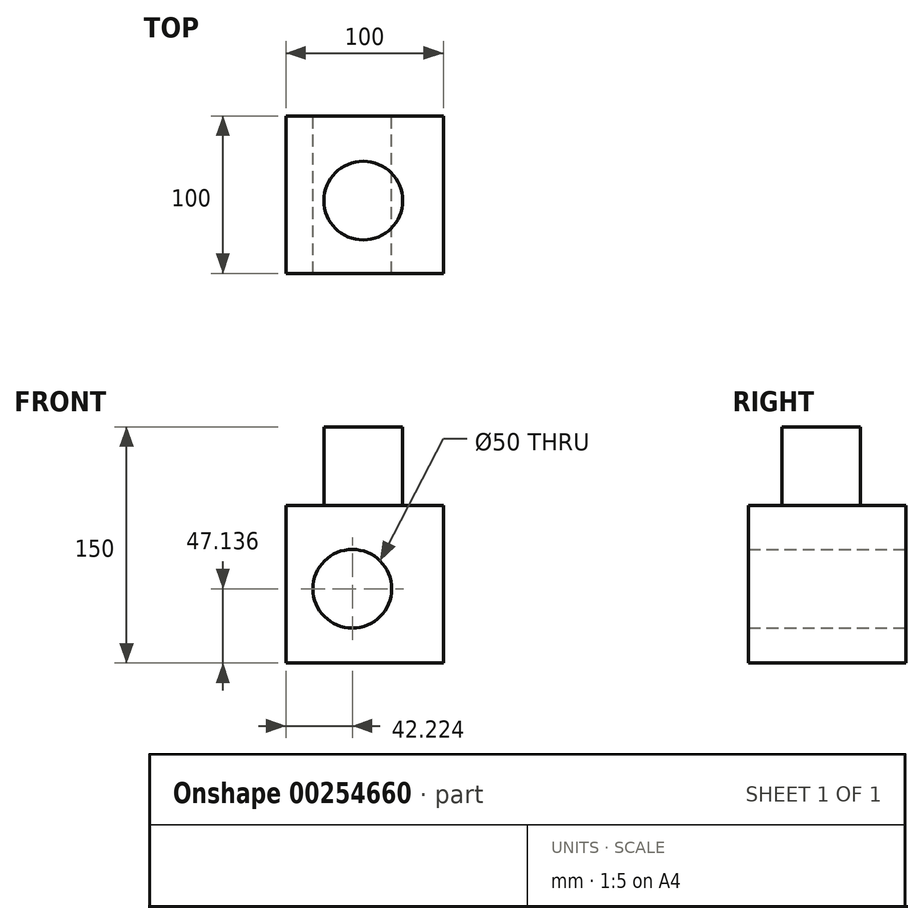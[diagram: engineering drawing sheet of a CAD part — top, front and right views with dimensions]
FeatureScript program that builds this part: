
annotation { "Feature Type Name" : "Feature", "Feature Type Description" : "" }
export const myFeature = defineFeature(function(context is Context, id is Id, definition is map)
    precondition{}
    {
        {
            var Q0;
            Q0=qCreatedBy(makeId("Front.planeOp"),FACE);
            var sketch = newSketch(context, id + "F0", { "sketchPlane" : qUnion([Q0])});
            skLineSegment(sketch, "E0.bottom", {"start": v(0, 0) * mm, "end": v(100, 0) * mm});
            skLineSegment(sketch, "E0.top", {"start": v(0, 100) * mm, "end": v(100, 100) * mm});
            skLineSegment(sketch, "E0.left", {"start": v(0, 0) * mm, "end": v(0, 100) * mm});
            skLineSegment(sketch, "E0.right", {"start": v(100, 0) * mm, "end": v(100, 100) * mm});
            skSolve(sketch);
        }
        {
            var Q0;
            Q0 = qSketchRegion(id + "F0", true);
            extrude(context, id + "F1", {"entities" : qUnion([Q0]), "depth" : 100 * mm});
        }
        {
            var Q0;
            Q0=makeQuery(id+"F1.opExtrude","SWEPT_FACE",FACE,{"disambiguationData":[OSD([sQuery(id+"F0.wireOp",EDGE,"E0.bottom")])]});
            var sketch = newSketch(context, id + "F2", { "sketchPlane" : qUnion([Q0])});
            skCircle(sketch, "E1", {"center": v(57.71, 56.55) * mm, "radius": 25 * mm});
            skCircle(sketch, "E2", {"center": v(43.51, 27.31) * mm, "radius": 25 * mm});
            skSolve(sketch);
        }
        {
            var Q0;
            Q0=sQuery(id+"F2.wireOp",EDGE,"E2");
            extrude(context, id + "F3", {"bodyType" : ToolBodyType.SURFACE, "surfaceEntities" : qUnion([Q0]), "depth" : 50 * mm});
        }
        {
            var Q0;
            Q0=makeQuery(id+"F1.opExtrude","SWEPT_FACE",FACE,{"disambiguationData":[OSD([sQuery(id+"F0.wireOp",EDGE,"E0.top")])]});
            var sketch = newSketch(context, id + "F4", { "sketchPlane" : qUnion([Q0])});
            skCircle(sketch, "E3", {"center": v(49.17, -53.8) * mm, "radius": 25 * mm});
            skSolve(sketch);
        }
        {
            var Q0;
            Q0 = qSketchRegion(id + "F4", true);
            extrude(context, id + "F5", {"entities" : qUnion([Q0]), "operationType" : NewBodyOperationType.ADD, "depth" : 50 * mm});
        }
        {
            var Q0;
            Q0=makeQuery(id+"F1.opExtrude","CAP_FACE",FACE,{"disambiguationData":[OSD([sQuery(id+"F0.wireOp",EDGE,"E0.bottom"),sQuery(id+"F0.wireOp",EDGE,"E0.top"),sQuery(id+"F0.wireOp",EDGE,"E0.left"),sQuery(id+"F0.wireOp",EDGE,"E0.right")])],"isStart":true});
            var sketch = newSketch(context, id + "F6", { "sketchPlane" : qUnion([Q0])});
            skCircle(sketch, "E4", {"center": v(-42, 47.15) * mm, "radius": 25 * mm});
            skSolve(sketch);
        }
        {
            var Q0;
            Q0=makeQuery(id+"F6.imprint","IMPRINT",FACE,{"disambiguationData":[TD([[makeQuery(id+"F6.imprint","IMPRINT",EDGE,{"derivedFrom":sQuery(id+"F6.wireOp",EDGE,"E4")}),1.0]])]});
            var sketch = newSketch(context, id + "F7", { "sketchPlane" : qUnion([Q0])});
            skPoint(sketch, "E5", {"position": v(-42.22, 47.14) * mm});
            skSolve(sketch);
        }
        {
            var Q0;
            Q0=sQuery(id+"F7.wireOp",VERTEX,"E5");
            var Q1;
            Q1=makeQuery(id+"F1.opExtrude","SWEPT_BODY",BODY,{"disambiguationData":[OSD([sQuery(id+"F0.wireOp",EDGE,"E0.bottom"),sQuery(id+"F0.wireOp",EDGE,"E0.top"),sQuery(id+"F0.wireOp",EDGE,"E0.left"),sQuery(id+"F0.wireOp",EDGE,"E0.right")])]});
            hole(context, id + "F8", {"style" : HoleStyle.SIMPLE, "endStyle" : HoleEndStyle.THROUGH, "holeDiameter" : 50 * mm, "tappedDepth" : 12 * mm, "tapClearance" : 3, "locations" : qUnion([Q0]), "scope" : qUnion([Q1])});
        }
    });
